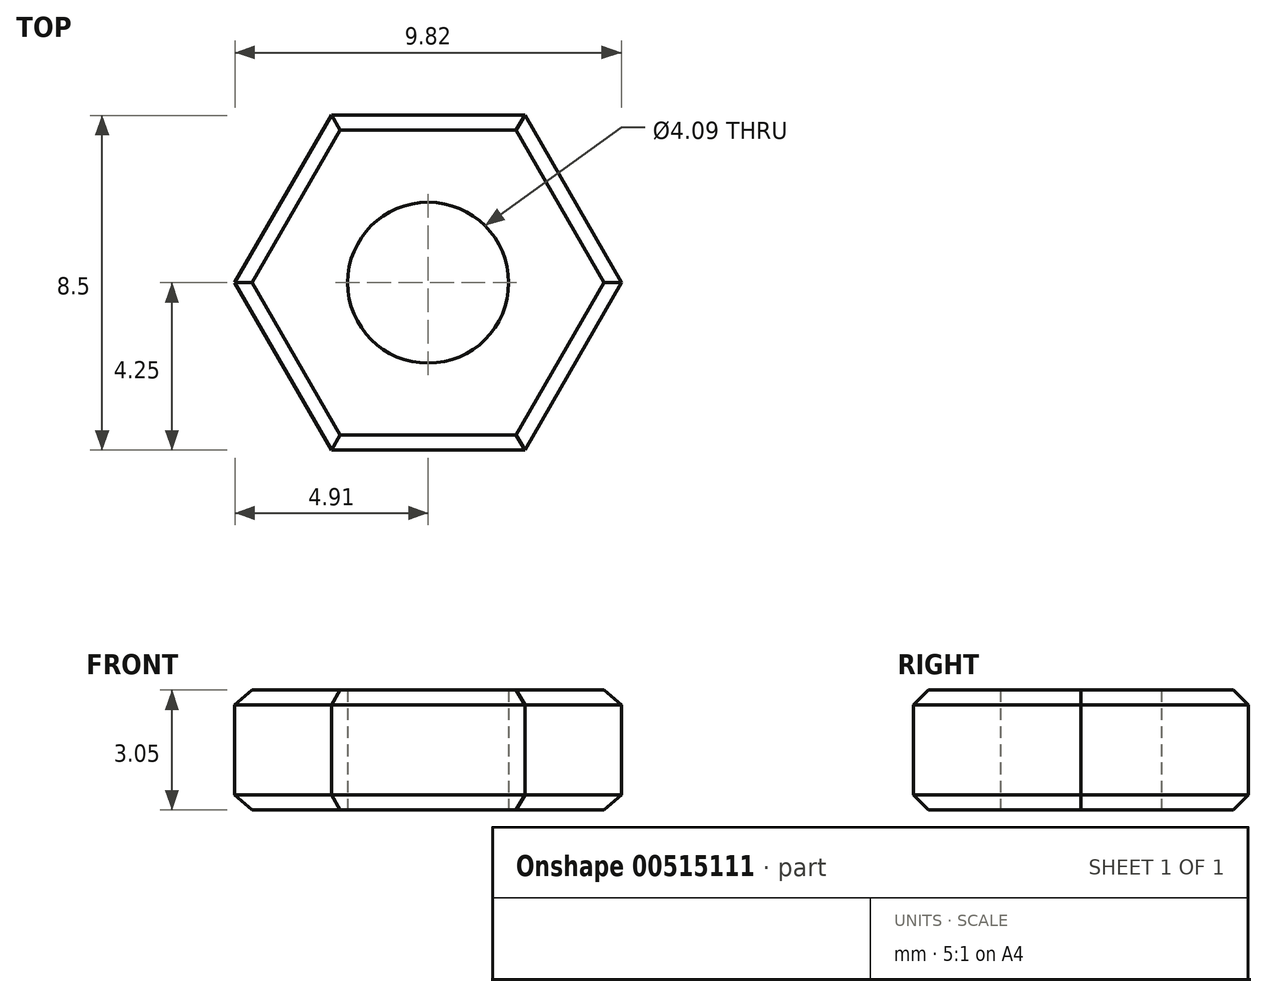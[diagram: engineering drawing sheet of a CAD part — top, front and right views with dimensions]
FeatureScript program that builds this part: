
annotation { "Feature Type Name" : "Feature", "Feature Type Description" : "" }
export const myFeature = defineFeature(function(context is Context, id is Id, definition is map)
    precondition{}
    {
        {
            var Q0;
            Q0=qCreatedBy(makeId("Top.planeOp"),FACE);
            var sketch = newSketch(context, id + "F0", { "sketchPlane" : qUnion([Q0])});
            skCircle(sketch, "E0.cCircle", {"center": v(0, 0) * mm, "radius": 4.25 * mm, "construction": true});
            skLineSegment(sketch, "E0.0", {"start": v(2.46, -4.25) * mm, "end": v(-2.46, -4.25) * mm});
            skLineSegment(sketch, "E0.1", {"start": v(-2.46, -4.25) * mm, "end": v(-4.91, 0) * mm});
            skLineSegment(sketch, "E0.2", {"start": v(-4.91, 0) * mm, "end": v(-2.46, 4.25) * mm});
            skLineSegment(sketch, "E0.3", {"start": v(-2.46, 4.25) * mm, "end": v(2.46, 4.25) * mm});
            skLineSegment(sketch, "E0.4", {"start": v(2.46, 4.25) * mm, "end": v(4.91, 0) * mm});
            skLineSegment(sketch, "E0.5", {"start": v(4.91, 0) * mm, "end": v(2.46, -4.25) * mm});
            skPoint(sketch, "E0.0.midPoint", {"position": v(0, -4.25) * mm});
            skCircle(sketch, "E1", {"center": v(0, 0) * mm, "radius": 2.04 * mm});
            skSolve(sketch);
        }
        {
            var Q0;
            Q0=makeQuery(id+"F0.imprint","IMPRINT",FACE,{"disambiguationData":[TD([[makeQuery(id+"F0.imprint","IMPRINT",EDGE,{"derivedFrom":sQuery(id+"F0.wireOp",EDGE,"E0.0")}),-1.0]])]});
            extrude(context, id + "F1", {"entities" : qUnion([Q0]), "depth" : 3.05 * mm, "offsetDistance" : 25.4 * mm});
        }
        {
            var Q0;
            Q0=makeQuery(id+"F1.opExtrude","CAP_EDGE",EDGE,{"disambiguationData":[OSD([sQuery(id+"F0.wireOp",EDGE,"E0.5")])],"isStart":false});
            var Q1;
            Q1=makeQuery(id+"F1.opExtrude","CAP_EDGE",EDGE,{"disambiguationData":[OSD([sQuery(id+"F0.wireOp",EDGE,"E0.0")])],"isStart":false});
            var Q2;
            Q2=makeQuery(id+"F1.opExtrude","CAP_EDGE",EDGE,{"disambiguationData":[OSD([sQuery(id+"F0.wireOp",EDGE,"E0.1")])],"isStart":false});
            var Q3;
            Q3=makeQuery(id+"F1.opExtrude","CAP_EDGE",EDGE,{"disambiguationData":[OSD([sQuery(id+"F0.wireOp",EDGE,"E0.2")])],"isStart":false});
            var Q4;
            Q4=makeQuery(id+"F1.opExtrude","CAP_EDGE",EDGE,{"disambiguationData":[OSD([sQuery(id+"F0.wireOp",EDGE,"E0.3")])],"isStart":false});
            var Q5;
            Q5=makeQuery(id+"F1.opExtrude","CAP_EDGE",EDGE,{"disambiguationData":[OSD([sQuery(id+"F0.wireOp",EDGE,"E0.4")])],"isStart":false});
            var Q6;
            Q6=makeQuery(id+"F1.opExtrude","CAP_EDGE",EDGE,{"disambiguationData":[OSD([sQuery(id+"F0.wireOp",EDGE,"E0.0")])],"isStart":true});
            var Q7;
            Q7=makeQuery(id+"F1.opExtrude","CAP_EDGE",EDGE,{"disambiguationData":[OSD([sQuery(id+"F0.wireOp",EDGE,"E0.1")])],"isStart":true});
            var Q8;
            Q8=makeQuery(id+"F1.opExtrude","CAP_EDGE",EDGE,{"disambiguationData":[OSD([sQuery(id+"F0.wireOp",EDGE,"E0.5")])],"isStart":true});
            var Q9;
            Q9=makeQuery(id+"F1.opExtrude","CAP_EDGE",EDGE,{"disambiguationData":[OSD([sQuery(id+"F0.wireOp",EDGE,"E0.4")])],"isStart":true});
            var Q10;
            Q10=makeQuery(id+"F1.opExtrude","CAP_EDGE",EDGE,{"disambiguationData":[OSD([sQuery(id+"F0.wireOp",EDGE,"E0.3")])],"isStart":true});
            var Q11;
            Q11=makeQuery(id+"F1.opExtrude","CAP_EDGE",EDGE,{"disambiguationData":[OSD([sQuery(id+"F0.wireOp",EDGE,"E0.2")])],"isStart":true});
            chamfer(context, id + "F2", {"entities" : qUnion([Q0, Q1, Q2, Q3, Q4, Q5, Q6, Q7, Q8, Q9, Q10, Q11]), "width" : 0.38 * mm, "tangentPropagation" : true});
        }
    });
